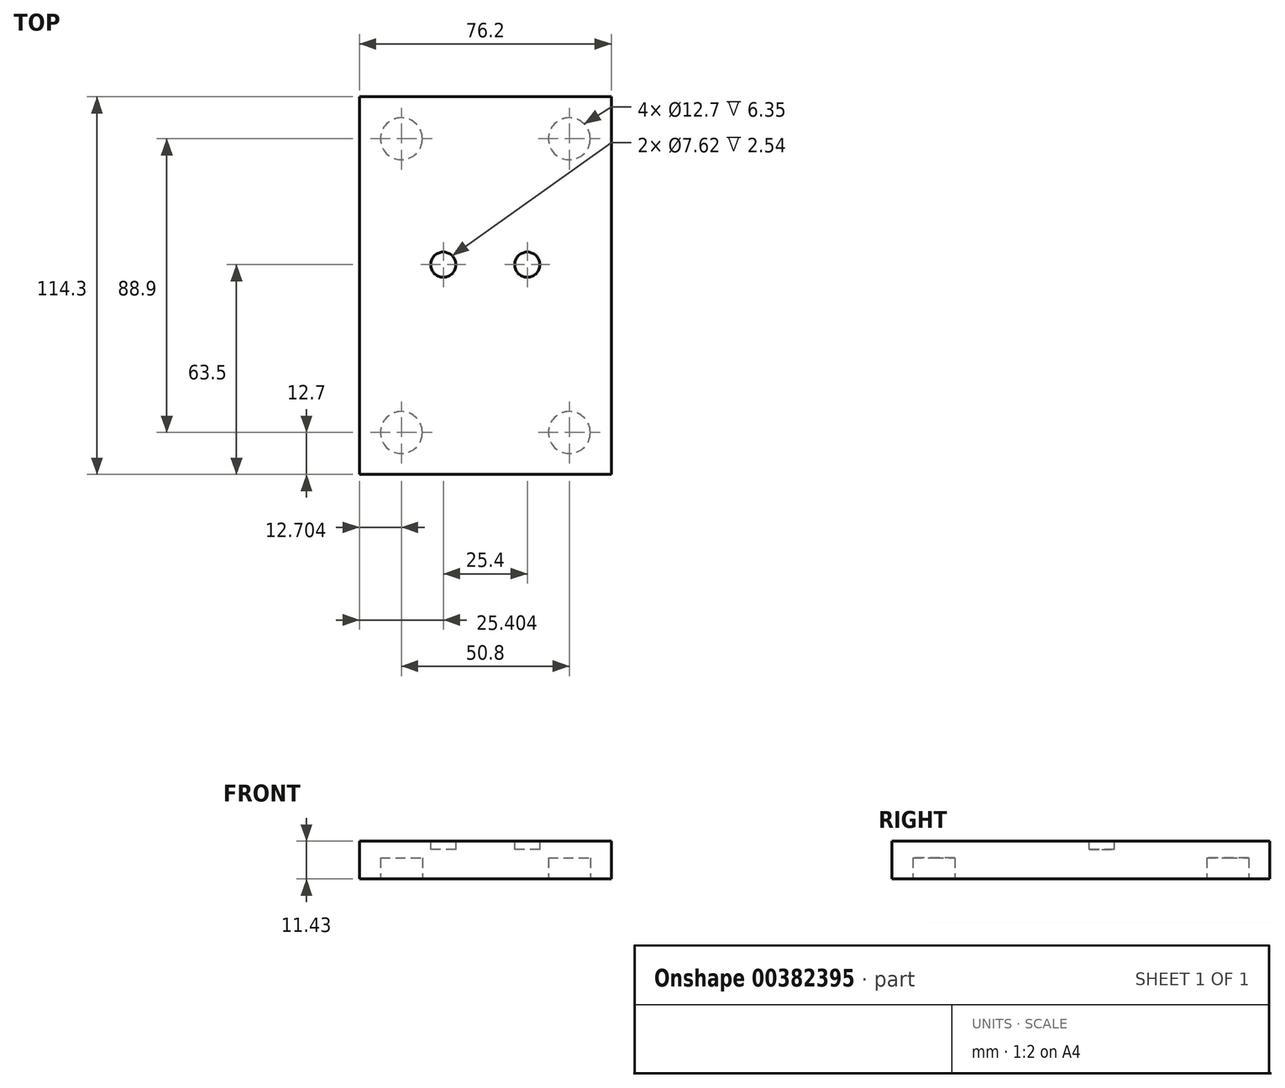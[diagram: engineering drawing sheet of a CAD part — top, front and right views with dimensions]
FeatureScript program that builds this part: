
annotation { "Feature Type Name" : "Feature", "Feature Type Description" : "" }
export const myFeature = defineFeature(function(context is Context, id is Id, definition is map)
    precondition{}
    {
        {
            var Q0;
            Q0=qCreatedBy(makeId("Front.planeOp"),FACE);
            var sketch = newSketch(context, id + "F0", { "sketchPlane" : qUnion([Q0])});
            skLineSegment(sketch, "E0.bottom", {"start": v(-34.34, -7.85) * mm, "end": v(41.86, -7.85) * mm});
            skLineSegment(sketch, "E0.top", {"start": v(-34.34, -19.28) * mm, "end": v(41.86, -19.28) * mm});
            skLineSegment(sketch, "E0.left", {"start": v(-34.34, -7.85) * mm, "end": v(-34.34, -19.28) * mm});
            skLineSegment(sketch, "E0.right", {"start": v(41.86, -7.85) * mm, "end": v(41.86, -19.28) * mm});
            skSolve(sketch);
        }
        {
            var Q0;
            Q0 = qSketchRegion(id + "F0", true);
            extrude(context, id + "F1", {"entities" : qUnion([Q0]), "depth" : 114.3 * mm});
        }
        {
            var Q0;
            Q0=makeQuery(id+"F1.opExtrude","SWEPT_FACE",FACE,{"disambiguationData":[OSD([sQuery(id+"F0.wireOp",EDGE,"E0.top")])]});
            var sketch = newSketch(context, id + "F2", { "sketchPlane" : qUnion([Q0])});
            skCircle(sketch, "E1", {"center": v(-21.64, 101.6) * mm, "radius": 6.35 * mm});
            skCircle(sketch, "E2", {"center": v(29.16, 101.6) * mm, "radius": 6.35 * mm});
            skCircle(sketch, "E3", {"center": v(29.16, 12.7) * mm, "radius": 6.35 * mm});
            skCircle(sketch, "E4", {"center": v(-21.64, 12.7) * mm, "radius": 6.35 * mm});
            skSolve(sketch);
        }
        {
            var Q0;
            Q0 = qSketchRegion(id + "F2", true);
            extrude(context, id + "F3", {"entities" : qUnion([Q0]), "operationType" : NewBodyOperationType.REMOVE, "oppositeDirection" : true, "depth" : 6.35 * mm});
        }
        {
            var Q0;
            Q0=makeQuery(id+"F1.opExtrude","SWEPT_FACE",FACE,{"disambiguationData":[OSD([sQuery(id+"F0.wireOp",EDGE,"E0.bottom")])]});
            var sketch = newSketch(context, id + "F4", { "sketchPlane" : qUnion([Q0])});
            skCircle(sketch, "E5", {"center": v(16.46, -50.8) * mm, "radius": 3.81 * mm});
            skCircle(sketch, "E6", {"center": v(-8.94, -50.8) * mm, "radius": 3.81 * mm});
            skSolve(sketch);
        }
        {
            var Q0;
            Q0 = qSketchRegion(id + "F4", true);
            extrude(context, id + "F5", {"entities" : qUnion([Q0]), "operationType" : NewBodyOperationType.REMOVE, "oppositeDirection" : true, "depth" : 2.54 * mm});
        }
    });
